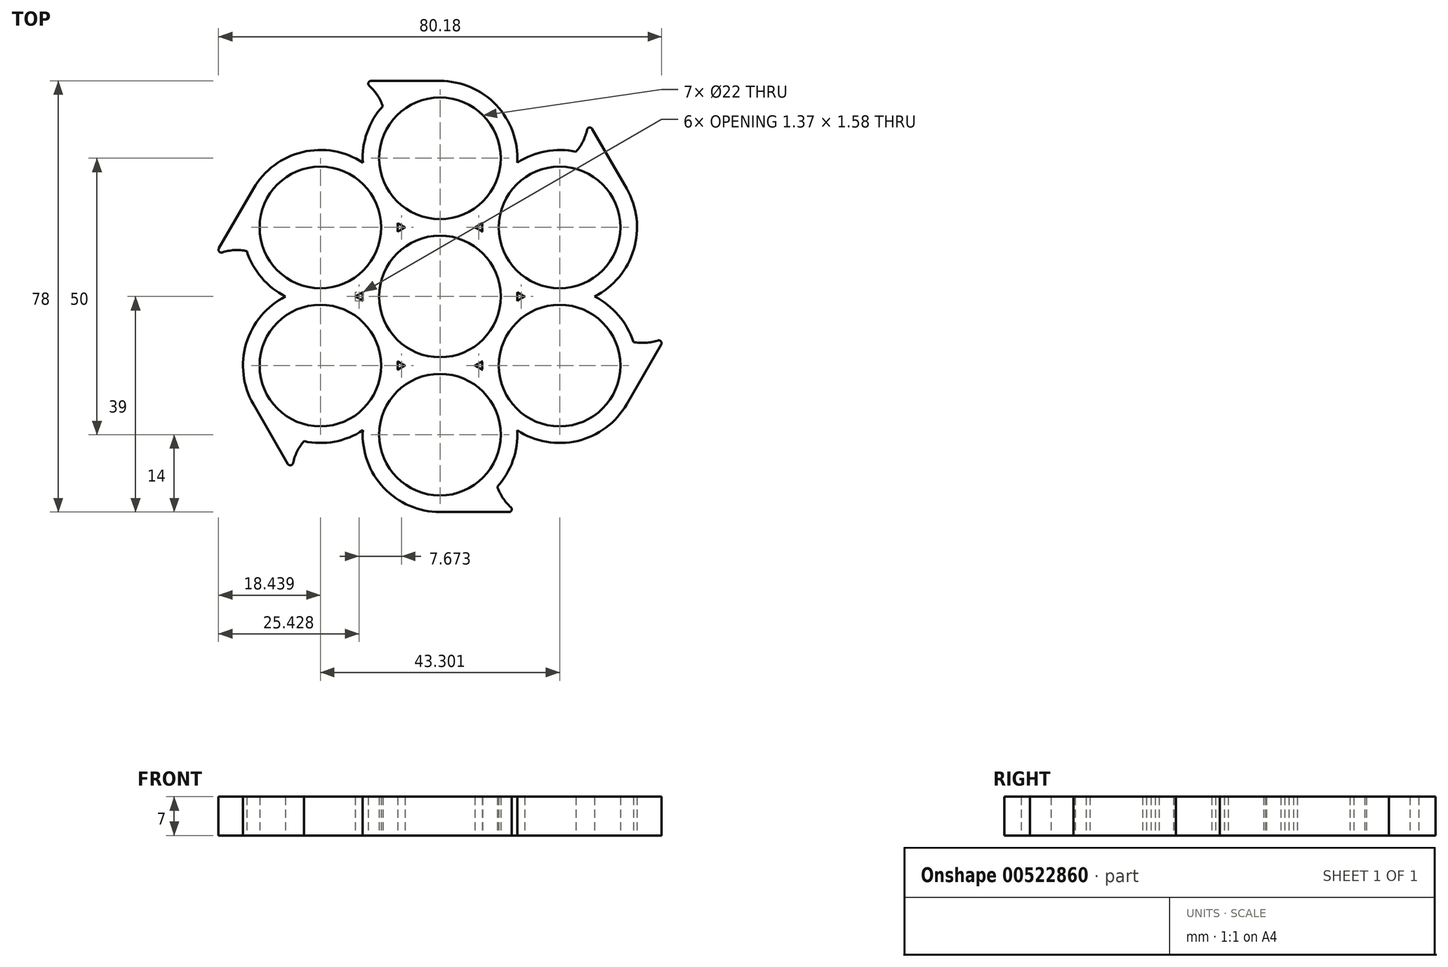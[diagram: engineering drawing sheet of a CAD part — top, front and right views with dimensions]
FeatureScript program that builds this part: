
annotation { "Feature Type Name" : "Feature", "Feature Type Description" : "" }
export const myFeature = defineFeature(function(context is Context, id is Id, definition is map)
    precondition{}
    {
        {
            var Q0;
            Q0=qCreatedBy(makeId("Top.planeOp"),FACE);
            var sketch = newSketch(context, id + "F0", { "sketchPlane" : qUnion([Q0])});
            skCircle(sketch, "E0", {"center": v(0, 0) * mm, "radius": 11 * mm});
            skArc(sketch, "E1", {"start": v(-13.98, 0.79) * mm, "mid": v(-14, 0) * mm, "end": v(-13.98, -0.79) * mm});
            skCircle(sketch, "E2", {"center": v(0, 25) * mm, "radius": 11 * mm});
            skArc(sketch, "E3", {"start": v(-7.67, 13.29) * mm, "mid": v(-7, 12.88) * mm, "end": v(-6.3, 12.5) * mm});
            skCircle(sketch, "E4.1.0", {"center": v(-21.65, 12.5) * mm, "radius": 11 * mm});
            skArc(sketch, "E4.1.1", {"start": v(-7.67, 11.71) * mm, "mid": v(-7.65, 12.5) * mm, "end": v(-7.67, 13.29) * mm});
            skCircle(sketch, "E4.2.0", {"center": v(-21.65, -12.5) * mm, "radius": 11 * mm});
            skArc(sketch, "E4.2.1", {"start": v(-7.67, -13.29) * mm, "mid": v(-7.65, -12.5) * mm, "end": v(-7.67, -11.71) * mm});
            skCircle(sketch, "E4.3.0", {"center": v(0, -25) * mm, "radius": 11 * mm});
            skArc(sketch, "E4.3.1", {"start": v(7.67, -13.29) * mm, "mid": v(7, -12.88) * mm, "end": v(6.3, -12.5) * mm});
            skCircle(sketch, "E4.4.0", {"center": v(21.65, -12.5) * mm, "radius": 11 * mm});
            skArc(sketch, "E4.4.1", {"start": v(7.67, -11.71) * mm, "mid": v(7.65, -12.5) * mm, "end": v(7.67, -13.29) * mm});
            skCircle(sketch, "E4.5.0", {"center": v(21.65, 12.5) * mm, "radius": 11 * mm});
            skArc(sketch, "E4.5.1", {"start": v(7.67, 13.29) * mm, "mid": v(7.65, 12.5) * mm, "end": v(7.67, 11.71) * mm});
            skArc(sketch, "E5.trimOffspring", {"start": v(-13.98, 24.21) * mm, "mid": v(-33.77, 19.5) * mm, "end": v(-27.96, 0) * mm});
            skArc(sketch, "E6.trimOffspring", {"start": v(-6.3, 12.5) * mm, "mid": v(-7, 12.12) * mm, "end": v(-7.67, 11.71) * mm});
            skArc(sketch, "E7.trimOffspring", {"start": v(6.3, 12.5) * mm, "mid": v(7, 12.88) * mm, "end": v(7.67, 13.29) * mm});
            skArc(sketch, "E8.trimOffspring", {"start": v(7.67, 11.71) * mm, "mid": v(7, 12.12) * mm, "end": v(6.3, 12.5) * mm});
            skArc(sketch, "E9.trimOffspring", {"start": v(13.98, 24.21) * mm, "mid": v(0, 39) * mm, "end": v(-13.98, 24.21) * mm});
            skArc(sketch, "E10.trimOffspring", {"start": v(13.98, 0.79) * mm, "mid": v(14.65, 0.38) * mm, "end": v(15.35, 0) * mm});
            skArc(sketch, "E11.trimOffspring", {"start": v(13.98, -0.79) * mm, "mid": v(14, 0) * mm, "end": v(13.98, 0.79) * mm});
            skArc(sketch, "E12.trimOffspring", {"start": v(27.96, 0) * mm, "mid": v(33.77, 19.5) * mm, "end": v(13.98, 24.21) * mm});
            skArc(sketch, "E13.trimOffspring", {"start": v(15.35, 0) * mm, "mid": v(14.65, -0.38) * mm, "end": v(13.98, -0.79) * mm});
            skArc(sketch, "E14.trimOffspring", {"start": v(13.98, -24.21) * mm, "mid": v(33.77, -19.5) * mm, "end": v(27.96, 0) * mm});
            skArc(sketch, "E15.trimOffspring", {"start": v(-6.3, -12.5) * mm, "mid": v(-7, -12.88) * mm, "end": v(-7.67, -13.29) * mm});
            skArc(sketch, "E16.trimOffspring", {"start": v(6.3, -12.5) * mm, "mid": v(7, -12.12) * mm, "end": v(7.67, -11.71) * mm});
            skArc(sketch, "E17.trimOffspring", {"start": v(-13.98, -24.21) * mm, "mid": v(0, -39) * mm, "end": v(13.98, -24.21) * mm});
            skArc(sketch, "E18.trimOffspring", {"start": v(-13.98, -0.79) * mm, "mid": v(-14.65, -0.38) * mm, "end": v(-15.35, 0) * mm});
            skArc(sketch, "E19.trimOffspring", {"start": v(-7.67, -11.71) * mm, "mid": v(-7, -12.12) * mm, "end": v(-6.3, -12.5) * mm});
            skArc(sketch, "E20.trimOffspring", {"start": v(-15.35, 0) * mm, "mid": v(-14.65, 0.38) * mm, "end": v(-13.98, 0.79) * mm});
            skArc(sketch, "E21.trimOffspring", {"start": v(-27.96, 0) * mm, "mid": v(-33.77, -19.5) * mm, "end": v(-13.98, -24.21) * mm});
            skPoint(sketch, "E22.1.internal.snap0", {"position": v(0, 39) * mm});
            skLineSegment(sketch, "E23", {"start": v(0, 39) * mm, "end": v(-12.49, 39) * mm});
            skArc(sketch, "E24", {"start": v(-10.36, 34.41) * mm, "mid": v(-11.35, 36.43) * mm, "end": v(-12.82, 38.13) * mm});
            skPoint(sketch, "E25.visualSharp", {"position": v(-13.98, 39) * mm});
            skArc(sketch, "E25.filletArc", {"start": v(-12.49, 39) * mm, "mid": v(-12.95, 38.68) * mm, "end": v(-12.82, 38.13) * mm});
            skArc(sketch, "E26.1.0", {"start": v(-34.98, 8.23) * mm, "mid": v(-37.22, 8.38) * mm, "end": v(-39.43, 7.96) * mm});
            skArc(sketch, "E26.1.1", {"start": v(-40.02, 8.69) * mm, "mid": v(-39.97, 8.12) * mm, "end": v(-39.43, 7.96) * mm});
            skLineSegment(sketch, "E26.1.2", {"start": v(-33.77, 19.5) * mm, "end": v(-40.02, 8.69) * mm});
            skArc(sketch, "E26.2.0", {"start": v(-24.62, -26.18) * mm, "mid": v(-25.87, -28.04) * mm, "end": v(-26.6, -30.17) * mm});
            skArc(sketch, "E26.2.1", {"start": v(-27.53, -30.31) * mm, "mid": v(-27.02, -30.56) * mm, "end": v(-26.6, -30.17) * mm});
            skLineSegment(sketch, "E26.2.2", {"start": v(-33.77, -19.5) * mm, "end": v(-27.53, -30.31) * mm});
            skArc(sketch, "E26.3.0", {"start": v(10.36, -34.41) * mm, "mid": v(11.35, -36.43) * mm, "end": v(12.82, -38.13) * mm});
            skArc(sketch, "E26.3.1", {"start": v(12.49, -39) * mm, "mid": v(12.95, -38.68) * mm, "end": v(12.82, -38.13) * mm});
            skLineSegment(sketch, "E26.3.2", {"start": v(0, -39) * mm, "end": v(12.49, -39) * mm});
            skArc(sketch, "E26.4.0", {"start": v(34.98, -8.23) * mm, "mid": v(37.22, -8.38) * mm, "end": v(39.43, -7.96) * mm});
            skArc(sketch, "E26.4.1", {"start": v(40.02, -8.69) * mm, "mid": v(39.97, -8.12) * mm, "end": v(39.43, -7.96) * mm});
            skLineSegment(sketch, "E26.4.2", {"start": v(33.77, -19.5) * mm, "end": v(40.02, -8.69) * mm});
            skArc(sketch, "E26.5.0", {"start": v(24.62, 26.18) * mm, "mid": v(25.87, 28.04) * mm, "end": v(26.6, 30.17) * mm});
            skArc(sketch, "E26.5.1", {"start": v(27.53, 30.31) * mm, "mid": v(27.02, 30.56) * mm, "end": v(26.6, 30.17) * mm});
            skLineSegment(sketch, "E26.5.2", {"start": v(33.77, 19.5) * mm, "end": v(27.53, 30.31) * mm});
            skSolve(sketch);
        }
        {
            var Q0;
            Q0 = qSketchRegion(id + "F0", true);
            extrude(context, id + "F1", {"entities" : qUnion([Q0]), "depth" : 7 * mm, "offsetDistance" : 25 * mm});
        }
    });
